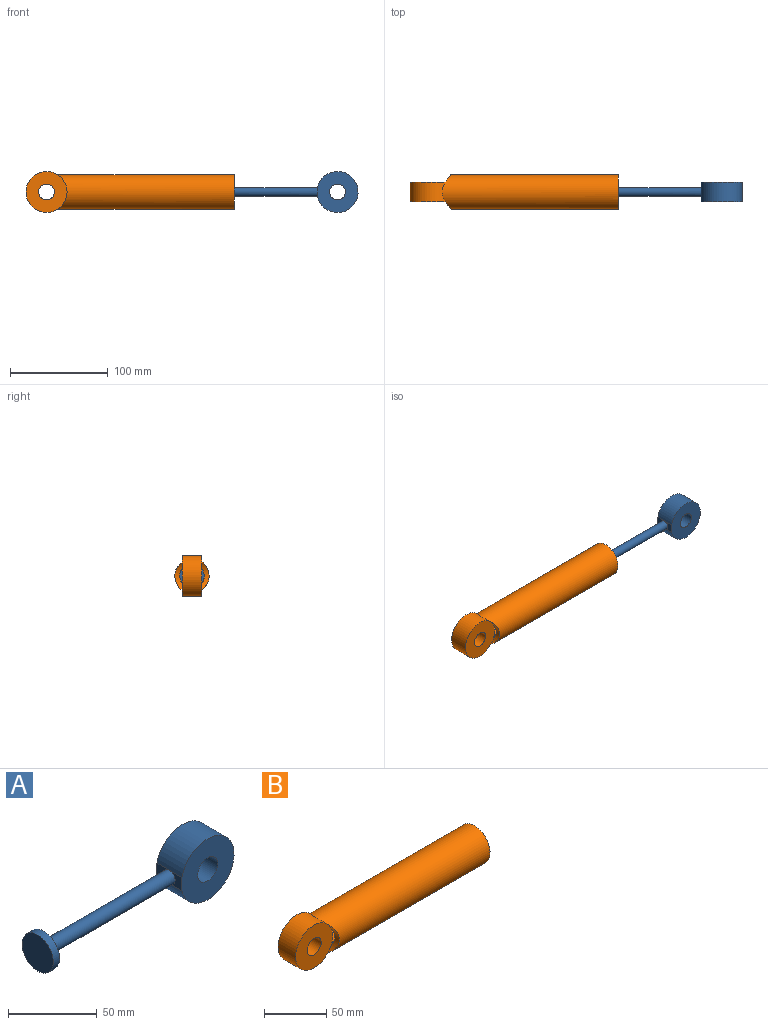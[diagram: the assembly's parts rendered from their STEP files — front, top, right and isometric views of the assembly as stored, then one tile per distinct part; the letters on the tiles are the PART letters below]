
ASSEMBLY  parts=2 mates=1
PART A: 10 faces, bbox 146.5x25x42 mm
  f0: cylinder r=4.52mm len=100mm, axis (-1,0,0), area 2841.5mm2, adj f3,f4,f7
  f1: cylinder r=12.5mm len=25mm, axis (1,0,0), area 392.7mm2, adj f2,f3
  f2: plane 25x25mm, normal (-1,0,0), area 490.9mm2, adj f1
  f3: plane 25x25mm, normal (1,0,0), area 426.6mm2, adj f0,f1
  f4: plane 10x9.04mm, normal (-1,0,0), area 58.3mm2, adj f0,f5,f9
  f5: cylinder r=21mm len=42mm, axis (0,1,0), area 2456.6mm2, adj f4,f7,f8,f9
  f6: cylinder r=8mm len=20mm, axis (0,1,0), area 1005.3mm2, adj f8,f9
  f7: plane 10x9.04mm, normal (-1,0,0), area 58.3mm2, adj f0,f5,f8
  f8: plane 42x41.51mm, normal (0,-1,0), area 1181.4mm2, adj f5,f6,f7
  f9: plane 42x41.51mm, normal (0,1,0), area 1181.4mm2, adj f4,f5,f6
PART B: 10 faces, bbox 213x35x42 mm
  f0: cylinder r=8mm len=20mm, axis (0,1,0), area 1005.3mm2, adj f7,f9
  f1: cylinder r=21mm len=42mm, axis (0,1,0), area 1877.5mm2, adj f4,f7,f9
  f2: cylinder r=21mm len=25mm, axis (0,1,0), area 464.4mm2, adj f3,f7,f9
  f3: cylinder r=12.5mm len=175.13mm, axis (-1,0,0), area 13587.9mm2, adj f2,f5,f6,f8
  f4: cylinder r=17.5mm len=180.4mm, axis (-1,0,0), area 19281.4mm2, adj f1,f5,f6,f8
  f5: plane 35x35mm, normal (1,0,0), area 471.2mm2, adj f3,f4
  f6: cylinder r=21mm len=28.72mm, axis (0,1,0), area 134.3mm2, adj f3,f4,f7
  f7: plane 42x42mm, normal (0,1,0), area 1184.4mm2, adj f0,f1,f2,f6
  f8: cylinder r=21mm len=28.72mm, axis (0,-1,0), area 134.3mm2, adj f3,f4,f9
  f9: plane 42x42mm, normal (0,-1,0), area 1184.4mm2, adj f0,f1,f2,f8
PLACE A t=(-30.41,-8.35,-99.75)mm
PLACE B rot(axis=(-1,0,0),0deg) t=(-93.41,-8.35,-30.35)mm
MATE slider B.f4 <-> A.f0  axis (-1,0,0) through (-15.41,-8.35,-30.35)mm
